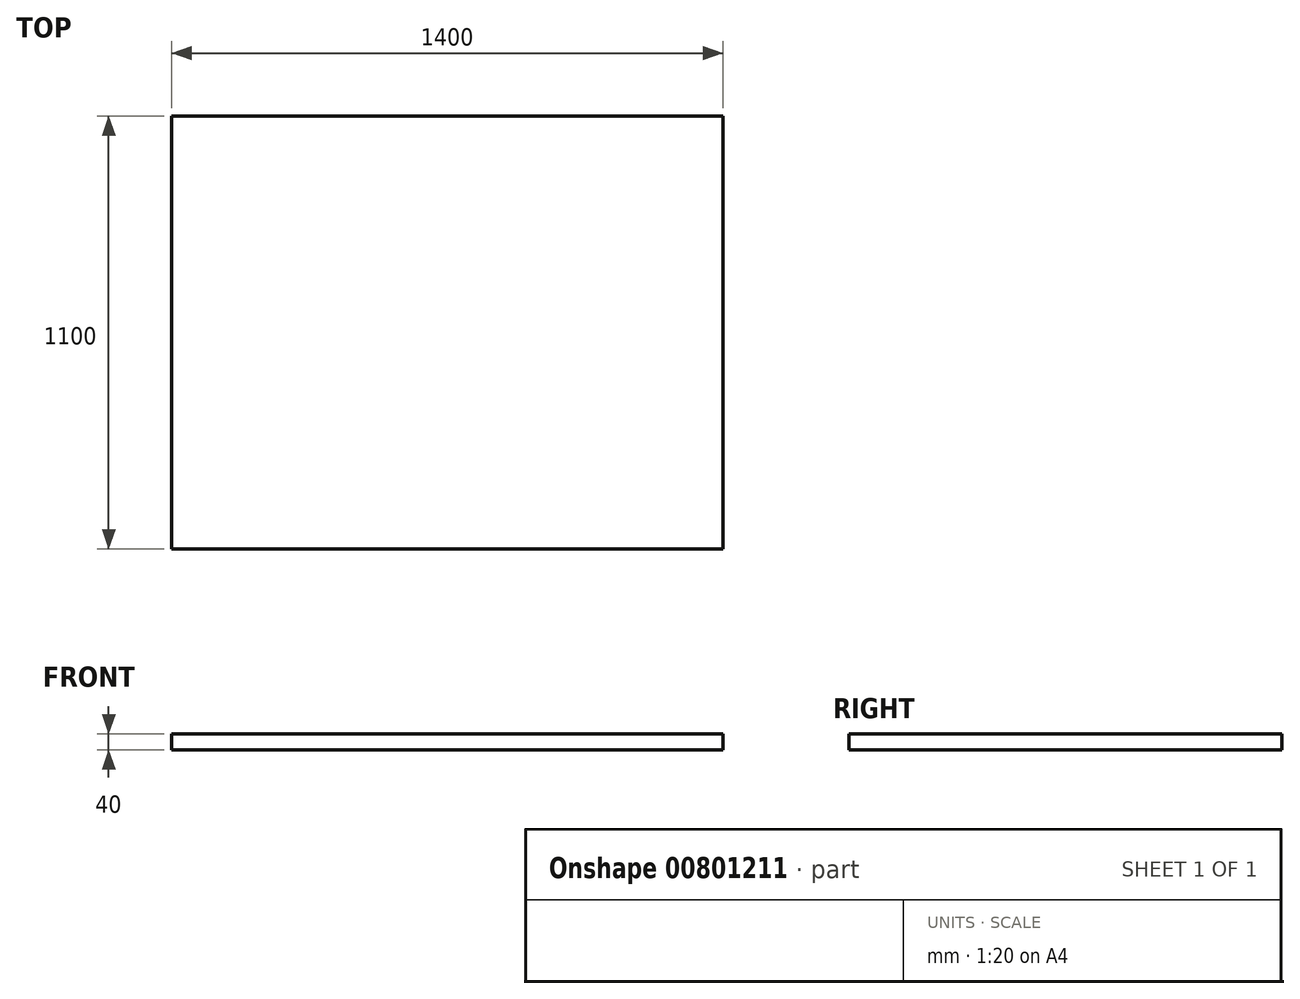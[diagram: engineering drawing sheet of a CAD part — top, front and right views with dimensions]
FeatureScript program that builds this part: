
annotation { "Feature Type Name" : "Feature", "Feature Type Description" : "" }
export const myFeature = defineFeature(function(context is Context, id is Id, definition is map)
    precondition{}
    {
        {
            var Q0;
            Q0=qCreatedBy(makeId("Top.planeOp"),FACE);
            var sketch = newSketch(context, id + "F0", { "sketchPlane" : qUnion([Q0])});
            skLineSegment(sketch, "E0.bottom", {"start": v(-700, 550) * mm, "end": v(700, 550) * mm});
            skLineSegment(sketch, "E0.top", {"start": v(-700, -550) * mm, "end": v(700, -550) * mm});
            skLineSegment(sketch, "E0.left", {"start": v(-700, 550) * mm, "end": v(-700, -550) * mm});
            skLineSegment(sketch, "E0.right", {"start": v(700, 550) * mm, "end": v(700, -550) * mm});
            skPoint(sketch, "E0.middle", {"position": v(0, 0) * mm});
            skSolve(sketch);
        }
        {
            var Q0;
            Q0 = qSketchRegion(id + "F0", true);
            var Q1;
            Q1=makeQuery(id+"F0.imprint","IMPRINT",FACE,{"disambiguationData":[TD([[makeQuery(id+"F0.imprint","IMPRINT",EDGE,{"derivedFrom":sQuery(id+"F0.wireOp",EDGE,"E0.bottom")}),-1.0]])]});
            extrude(context, id + "F1", {"entities" : qUnion([Q0, Q1]), "depth" : 40 * mm, "offsetDistance" : 25 * mm});
        }
    });
